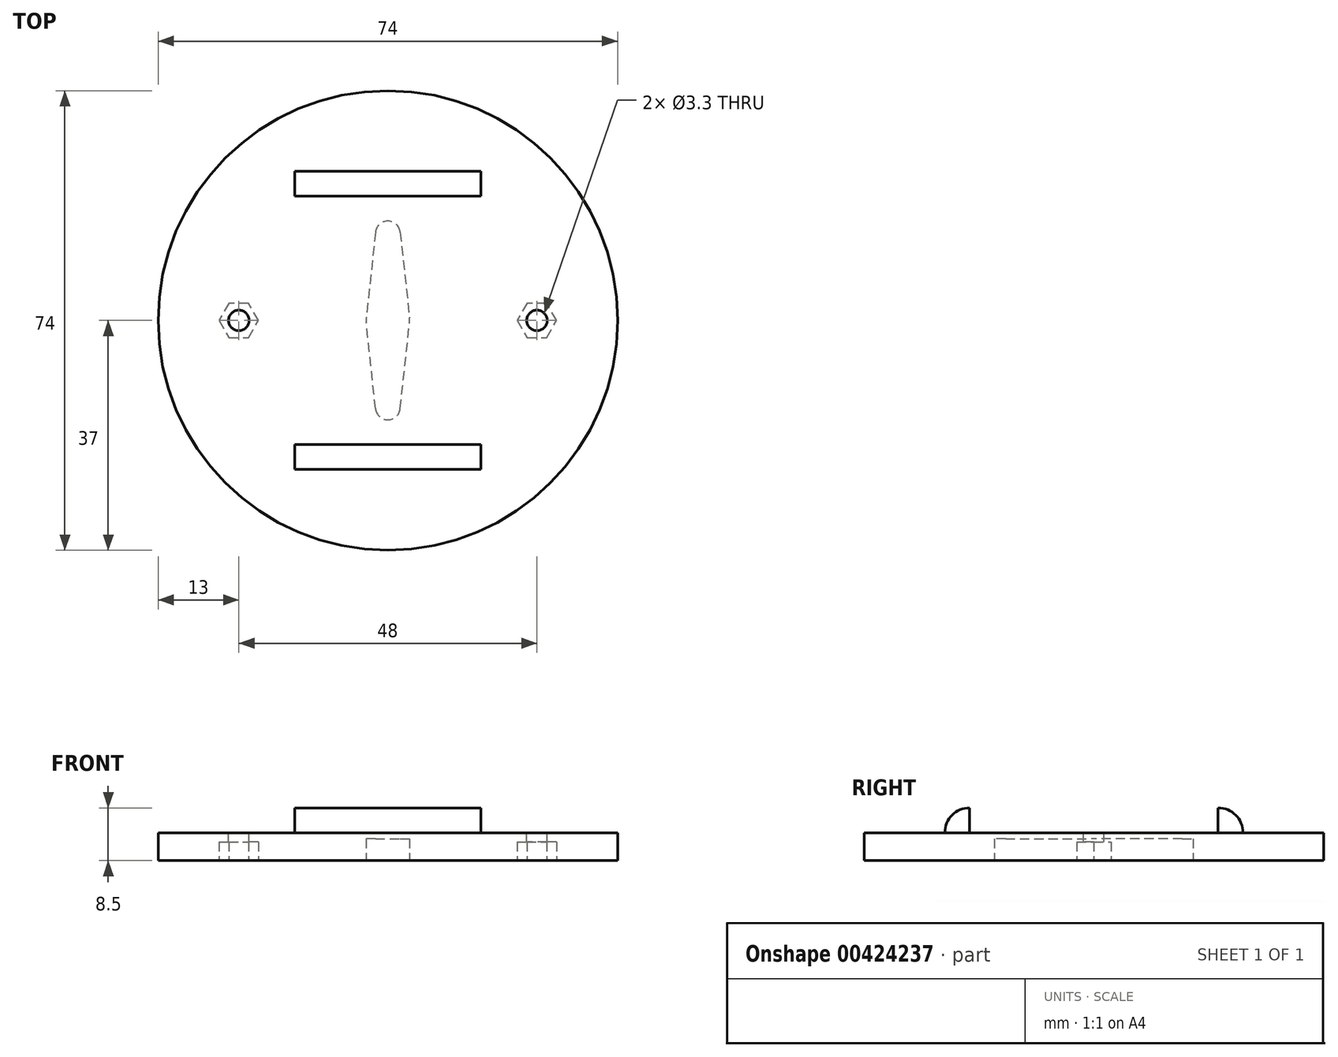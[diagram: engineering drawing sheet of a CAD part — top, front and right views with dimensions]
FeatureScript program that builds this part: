
annotation { "Feature Type Name" : "Feature", "Feature Type Description" : "" }
export const myFeature = defineFeature(function(context is Context, id is Id, definition is map)
    precondition{}
    {
        {
            var Q0;
            Q0=qCreatedBy(makeId("Top.planeOp"),FACE);
            var sketch = newSketch(context, id + "F0", { "sketchPlane" : qUnion([Q0])});
            skCircle(sketch, "E0", {"center": v(0, 0) * mm, "radius": 37 * mm});
            skSolve(sketch);
        }
        {
            var Q0;
            Q0=makeQuery(id+"F0.imprint","IMPRINT",FACE,{"disambiguationData":[TD([[makeQuery(id+"F0.imprint","IMPRINT",EDGE,{"derivedFrom":sQuery(id+"F0.wireOp",EDGE,"E0")}),1.0]])]});
            extrude(context, id + "F1", {"entities" : qUnion([Q0]), "depth" : 4.5 * mm});
        }
        {
            var Q0;
            Q0=makeQuery(id+"F1.opExtrude","CAP_FACE",FACE,{"disambiguationData":[OSD([sQuery(id+"F0.wireOp",EDGE,"E0")])],"isStart":true});
            var sketch = newSketch(context, id + "F2", { "sketchPlane" : qUnion([Q0])});
            skCircle(sketch, "E1", {"center": v(0, 0) * mm, "radius": 3.5 * mm});
            skLineSegment(sketch, "E2", {"start": v(0, 0) * mm, "end": v(0, 14) * mm});
            skCircle(sketch, "E3", {"center": v(0, 14) * mm, "radius": 2 * mm});
            skCircle(sketch, "E4.MirrorC", {"center": v(0, -14) * mm, "radius": 2 * mm});
            skLineSegment(sketch, "E5", {"start": v(-1.99, 14.21) * mm, "end": v(-3.48, 0.38) * mm});
            skLineSegment(sketch, "E6", {"start": v(1.99, 14.21) * mm, "end": v(3.48, 0.37) * mm});
            skLineSegment(sketch, "E7.MirrorCS", {"start": v(-1.99, -14.21) * mm, "end": v(-3.48, -0.38) * mm});
            skLineSegment(sketch, "E8.MirrorCS", {"start": v(1.99, -14.21) * mm, "end": v(3.48, -0.37) * mm});
            skSolve(sketch);
        }
        {
            var Q0;
            Q0=qSketchRegion(id+"F2",true);
            extrude(context, id + "F3", {"entities" : qUnion([Q0]), "operationType" : NewBodyOperationType.REMOVE, "oppositeDirection" : true, "depth" : 3.5 * mm});
        }
        {
            var Q0;
            Q0=qCreatedBy(makeId("Right.planeOp"),FACE);
            var sketch = newSketch(context, id + "F4", { "sketchPlane" : qUnion([Q0])});
            skLineSegment(sketch, "E9.0", {"start": v(-37, 4.5) * mm, "end": v(37, 4.5) * mm});
            skLineSegment(sketch, "E10", {"start": v(20, 4.5) * mm, "end": v(20, 8.5) * mm});
            skArc(sketch, "E11", {"start": v(20, 8.5) * mm, "mid": v(22.83, 7.33) * mm, "end": v(24, 4.5) * mm});
            skLineSegment(sketch, "E12.MirrorCS", {"start": v(-20, 4.5) * mm, "end": v(-20, 8.5) * mm});
            skArc(sketch, "E13.MirrorCS", {"start": v(-20, 8.5) * mm, "mid": v(-22.83, 7.33) * mm, "end": v(-24, 4.5) * mm});
            skSolve(sketch);
        }
        {
            var Q0;
            {var subQ0=sQuery(id+"F4.wireOp",EDGE,"E12.MirrorCS");Q0=makeQuery(id+"F4.imprint","IMPRINT",FACE,{"disambiguationData":[TD([[makeQuery(id+"F4.imprint","IMPRINT",EDGE,{"derivedFrom":subQ0}),1.0]])]});}
            var Q1;
            {var subQ0=sQuery(id+"F4.wireOp",EDGE,"E10");Q1=makeQuery(id+"F4.imprint","IMPRINT",FACE,{"disambiguationData":[TD([[makeQuery(id+"F4.imprint","IMPRINT",EDGE,{"derivedFrom":subQ0}),-1.0]])]});}
            extrude(context, id + "F5", {"entities" : qUnion([Q0, Q1]), "operationType" : NewBodyOperationType.ADD, "endBound" : BoundingType.SYMMETRIC, "depth" : 30 * mm});
        }
        {
            var Q0;
            Q0=makeQuery(id+"F1.opExtrude","CAP_FACE",FACE,{"disambiguationData":[OSD([sQuery(id+"F0.wireOp",EDGE,"E0")])],"isStart":false});
            var sketch = newSketch(context, id + "F6", { "sketchPlane" : qUnion([Q0])});
            skCircle(sketch, "E14", {"center": v(-24, 0) * mm, "radius": 1.65 * mm});
            skCircle(sketch, "E15.MirrorC", {"center": v(24, 0) * mm, "radius": 1.65 * mm});
            skSolve(sketch);
        }
        {
            var Q0;
            Q0=qSketchRegion(id+"F6",true);
            extrude(context, id + "F7", {"entities" : qUnion([Q0]), "operationType" : NewBodyOperationType.REMOVE, "endBound" : BoundingType.THROUGH_ALL, "oppositeDirection" : true, "depth" : 25 * mm});
        }
        {
            var Q0;
            Q0=makeQuery(id+"F1.opExtrude","CAP_FACE",FACE,{"disambiguationData":[OSD([sQuery(id+"F0.wireOp",EDGE,"E0")])],"isStart":true});
            var sketch = newSketch(context, id + "F8", { "sketchPlane" : qUnion([Q0])});
            skCircle(sketch, "E16.cCircle", {"center": v(24, 0) * mm, "radius": 2.75 * mm, "construction": true});
            skLineSegment(sketch, "E16.0", {"start": v(20.82, 0) * mm, "end": v(22.41, 2.75) * mm});
            skLineSegment(sketch, "E16.1", {"start": v(22.41, 2.75) * mm, "end": v(25.59, 2.75) * mm});
            skLineSegment(sketch, "E16.2", {"start": v(25.59, 2.75) * mm, "end": v(27.18, 0) * mm});
            skLineSegment(sketch, "E16.3", {"start": v(27.18, 0) * mm, "end": v(25.59, -2.75) * mm});
            skLineSegment(sketch, "E16.4", {"start": v(25.59, -2.75) * mm, "end": v(22.41, -2.75) * mm});
            skLineSegment(sketch, "E16.5", {"start": v(22.41, -2.75) * mm, "end": v(20.82, 0) * mm});
            skPoint(sketch, "E16.0.midPoint", {"position": v(21.62, 1.38) * mm});
            skLineSegment(sketch, "E17", {"start": v(20.82, 0) * mm, "end": v(27.18, 0) * mm, "construction": true});
            skCircle(sketch, "E18.cCircle", {"center": v(-24, 0) * mm, "radius": 2.75 * mm, "construction": true});
            skLineSegment(sketch, "E18.0", {"start": v(-20.82, 0) * mm, "end": v(-22.41, -2.75) * mm});
            skLineSegment(sketch, "E18.1", {"start": v(-22.41, -2.75) * mm, "end": v(-25.59, -2.75) * mm});
            skLineSegment(sketch, "E18.2", {"start": v(-25.59, -2.75) * mm, "end": v(-27.18, 0) * mm});
            skLineSegment(sketch, "E18.3", {"start": v(-27.18, 0) * mm, "end": v(-25.59, 2.75) * mm});
            skLineSegment(sketch, "E18.4", {"start": v(-25.59, 2.75) * mm, "end": v(-22.41, 2.75) * mm});
            skLineSegment(sketch, "E18.5", {"start": v(-22.41, 2.75) * mm, "end": v(-20.82, 0) * mm});
            skPoint(sketch, "E18.0.midPoint", {"position": v(-21.62, -1.38) * mm});
            skLineSegment(sketch, "E19", {"start": v(-20.82, 0) * mm, "end": v(-27.18, 0) * mm, "construction": true});
            skSolve(sketch);
        }
        {
            var Q0;
            Q0=qSketchRegion(id+"F8",true);
            extrude(context, id + "F9", {"entities" : qUnion([Q0]), "operationType" : NewBodyOperationType.REMOVE, "oppositeDirection" : true, "depth" : 3 * mm});
        }
    });
